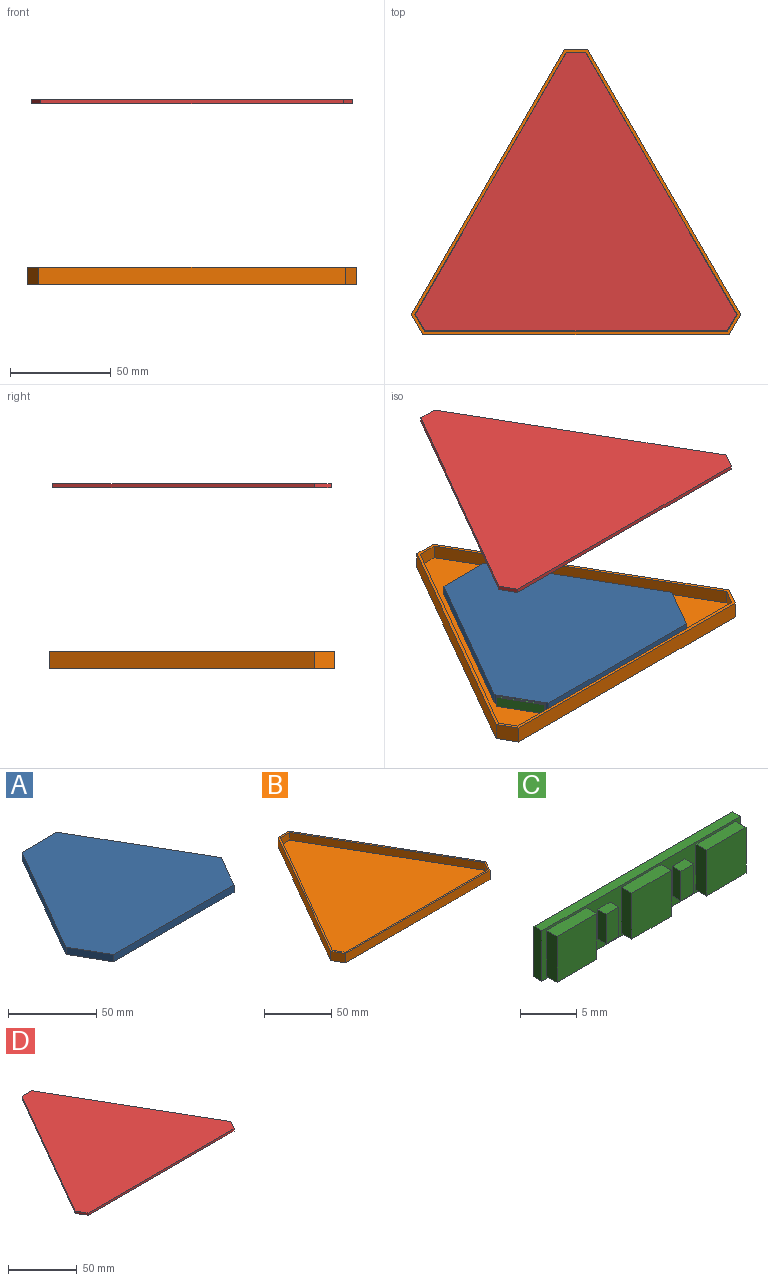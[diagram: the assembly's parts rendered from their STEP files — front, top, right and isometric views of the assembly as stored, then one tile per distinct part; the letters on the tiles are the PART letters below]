
ASSEMBLY  parts=4 mates=3
PART A: 8 faces, bbox 124.5x107.8x5 mm
  f0: plane 24.25x14mm, normal (0.87,-0.5,0), area 140mm2, adj f1,f5,f6,f7
  f1: plane 83.55x48.24mm, normal (0.87,0.5,0), area 482.4mm2, adj f0,f2,f6,f7
  f2: plane 28x5mm, normal (0,1,0), area 140mm2, adj f1,f3,f6,f7
  f3: plane 83.55x48.24mm, normal (-0.87,0.5,0), area 482.4mm2, adj f2,f4,f6,f7
  f4: plane 24.25x14mm, normal (-0.87,-0.5,0), area 140mm2, adj f3,f5,f6,f7
  f5: plane 96.48x5mm, normal (0,-1,0), area 482.4mm2, adj f0,f4,f6,f7
  f6: plane 124.48x107.8mm, normal (0,0,1), area 9049.4mm2, adj f0,f1,f2,f3,f4,f5
  f7: plane 124.48x107.8mm, normal (0,0,-1), area 9049.4mm2, adj f0,f1,f2,f3,f4,f5
PART B: 15 faces, bbox 163.5x141.6x8.5 mm
  f0: plane 11.55x8.5mm, normal (0,1,0), area 98.1mm2, adj f1,f5,f6,f13
  f1: plane 131.55x75.95mm, normal (-0.87,0.5,0), area 1291.2mm2, adj f0,f2,f6,f13
  f2: plane 10x8.5mm, normal (-0.87,-0.5,0), area 98.1mm2, adj f1,f3,f6,f13
  f3: plane 151.91x8.5mm, normal (0,-1,0), area 1291.2mm2, adj f2,f4,f6,f13
  f4: plane 10x8.5mm, normal (0.87,-0.5,0), area 98.1mm2, adj f3,f5,f6,f13
  f5: plane 131.55x75.95mm, normal (0.87,0.5,0), area 1291.2mm2, adj f0,f4,f6,f13
  f6: plane 163.45x141.55mm, normal (0,0,-1), area 13087.8mm2, adj f0,f1,f2,f3,f4,f5
  f7: plane 8.5x7mm, normal (0.87,0.5,0), area 68.7mm2, adj f8,f12,f13,f14
  f8: plane 130.05x75.09mm, normal (0.87,-0.5,0), area 1051.2mm2, adj f7,f9,f13,f14
  f9: plane 9.82x7mm, normal (0,-1,0), area 68.7mm2, adj f8,f10,f13,f14
  f10: plane 130.05x75.09mm, normal (-0.87,-0.5,0), area 1051.2mm2, adj f9,f11,f13,f14
  f11: plane 8.5x7mm, normal (-0.87,0.5,0), area 68.7mm2, adj f10,f12,f13,f14
  f12: plane 150.17x7mm, normal (0,1,0), area 1051.2mm2, adj f7,f11,f13,f14
  f13: plane 163.45x141.55mm, normal (0,0,1), area 727.7mm2, adj f0,f1,f2,f3,f4,f5,f7,f8
  f14: plane 159.99x138.55mm, normal (0,0,1), area 12360.1mm2, adj f7,f8,f9,f10,f11,f12
PART C: 31 faces, bbox 25x2.3x5.5 mm
  f0: plane 25x5.5mm, normal (0,-1,0), area 52.3mm2, adj f1,f2,f3,f4,f6,f7,f8,f9
  f1: plane 25x1mm, normal (0,0,-1), area 25mm2, adj f0,f2,f4,f5
  f2: plane 5.5x1mm, normal (1,0,0), area 5.5mm2, adj f0,f1,f3,f5
  f3: plane 25x1mm, normal (0,0,1), area 25mm2, adj f0,f2,f4,f5
  f4: plane 5.5x1mm, normal (-1,0,0), area 5.5mm2, adj f0,f1,f3,f5
  f5: plane 25x5.5mm, normal (0,1,0), area 137.5mm2, adj f1,f2,f3,f4
  f6: plane 5x1.3mm, normal (0,0,-1), area 6.5mm2, adj f0,f7,f9,f10
  f7: plane 5x1.3mm, normal (1,0,0), area 6.5mm2, adj f0,f6,f8,f10
  f8: plane 5x1.3mm, normal (0,0,1), area 6.5mm2, adj f0,f7,f9,f10
  f9: plane 5x1.3mm, normal (-1,0,0), area 6.5mm2, adj f0,f6,f8,f10
  f10: plane 5x5mm, normal (0,-1,0), area 25mm2, adj f6,f7,f8,f9
  f11: plane 5x1.3mm, normal (0,0,-1), area 6.5mm2, adj f0,f12,f14,f15
  f12: plane 5x1.3mm, normal (1,0,0), area 6.5mm2, adj f0,f11,f13,f15
  f13: plane 5x1.3mm, normal (0,0,1), area 6.5mm2, adj f0,f12,f14,f15
  f14: plane 5x1.3mm, normal (-1,0,0), area 6.5mm2, adj f0,f11,f13,f15
  f15: plane 5x5mm, normal (0,-1,0), area 25mm2, adj f11,f12,f13,f14
  f16: plane 5x1.3mm, normal (0,0,-1), area 6.5mm2, adj f0,f17,f19,f20
  f17: plane 5x1.3mm, normal (1,0,0), area 6.5mm2, adj f0,f16,f18,f20
  f18: plane 5x1.3mm, normal (0,0,1), area 6.5mm2, adj f0,f17,f19,f20
  f19: plane 5x1.3mm, normal (-1,0,0), area 6.5mm2, adj f0,f16,f18,f20
  f20: plane 5x5mm, normal (0,-1,0), area 25mm2, adj f16,f17,f18,f19
  f21: plane 1.6x1.1mm, normal (0,0,-1), area 1.8mm2, adj f0,f22,f24,f25
  f22: plane 3.2x1.1mm, normal (1,0,0), area 3.5mm2, adj f0,f21,f23,f25
  f23: plane 1.6x1.1mm, normal (0,0,1), area 1.8mm2, adj f0,f22,f24,f25
  f24: plane 3.2x1.1mm, normal (-1,0,0), area 3.5mm2, adj f0,f21,f23,f25
  f25: plane 3.2x1.6mm, normal (0,-1,0), area 5.1mm2, adj f21,f22,f23,f24
  f26: plane 1.6x1.1mm, normal (0,0,-1), area 1.8mm2, adj f0,f27,f29,f30
  f27: plane 3.2x1.1mm, normal (1,0,0), area 3.5mm2, adj f0,f26,f28,f30
  f28: plane 1.6x1.1mm, normal (0,0,1), area 1.8mm2, adj f0,f27,f29,f30
  f29: plane 3.2x1.1mm, normal (-1,0,0), area 3.5mm2, adj f0,f26,f28,f30
  f30: plane 3.2x1.6mm, normal (0,-1,0), area 5.1mm2, adj f26,f27,f28,f29
PART D: 8 faces, bbox 159.4x138.1x2 mm
  f0: plane 129.8x74.94mm, normal (-0.87,0.5,0), area 299.8mm2, adj f1,f5,f6,f7
  f1: plane 8.25x4.76mm, normal (-0.87,-0.5,0), area 19.1mm2, adj f0,f2,f6,f7
  f2: plane 149.89x2mm, normal (0,-1,0), area 299.8mm2, adj f1,f3,f6,f7
  f3: plane 8.25x4.76mm, normal (0.87,-0.5,0), area 19.1mm2, adj f2,f4,f6,f7
  f4: plane 129.8x74.94mm, normal (0.87,0.5,0), area 299.8mm2, adj f3,f5,f6,f7
  f5: plane 9.53x2mm, normal (0,1,0), area 19.1mm2, adj f0,f4,f6,f7
  f6: plane 159.41x138.05mm, normal (0,0,1), area 12240.3mm2, adj f0,f1,f2,f3,f4,f5
  f7: plane 159.41x138.05mm, normal (0,0,-1), area 12240.3mm2, adj f0,f1,f2,f3,f4,f5
PLACE A t=(-1.78,-15.34,6.17)mm
PLACE B t=(-1.78,-15.34,6.17)mm fixed
PLACE C rot(axis=(0,0,1),120deg) t=(-58.15,-47.88,8.67)mm
PLACE D t=(-1.78,-15.34,94.11)mm
MATE fastened C.f15 <-> A.f4  axis (0.87,0.5,0) through (-57.02,-47.23,8.67)mm
MATE slider B.f14 <-> A.f7  axis (0,0,-1) through (-1.78,-15.34,6.17)mm
MATE slider A.f6 <-> D.f7  axis (0,0,-1) through (-1.78,-15.34,11.17)mm
